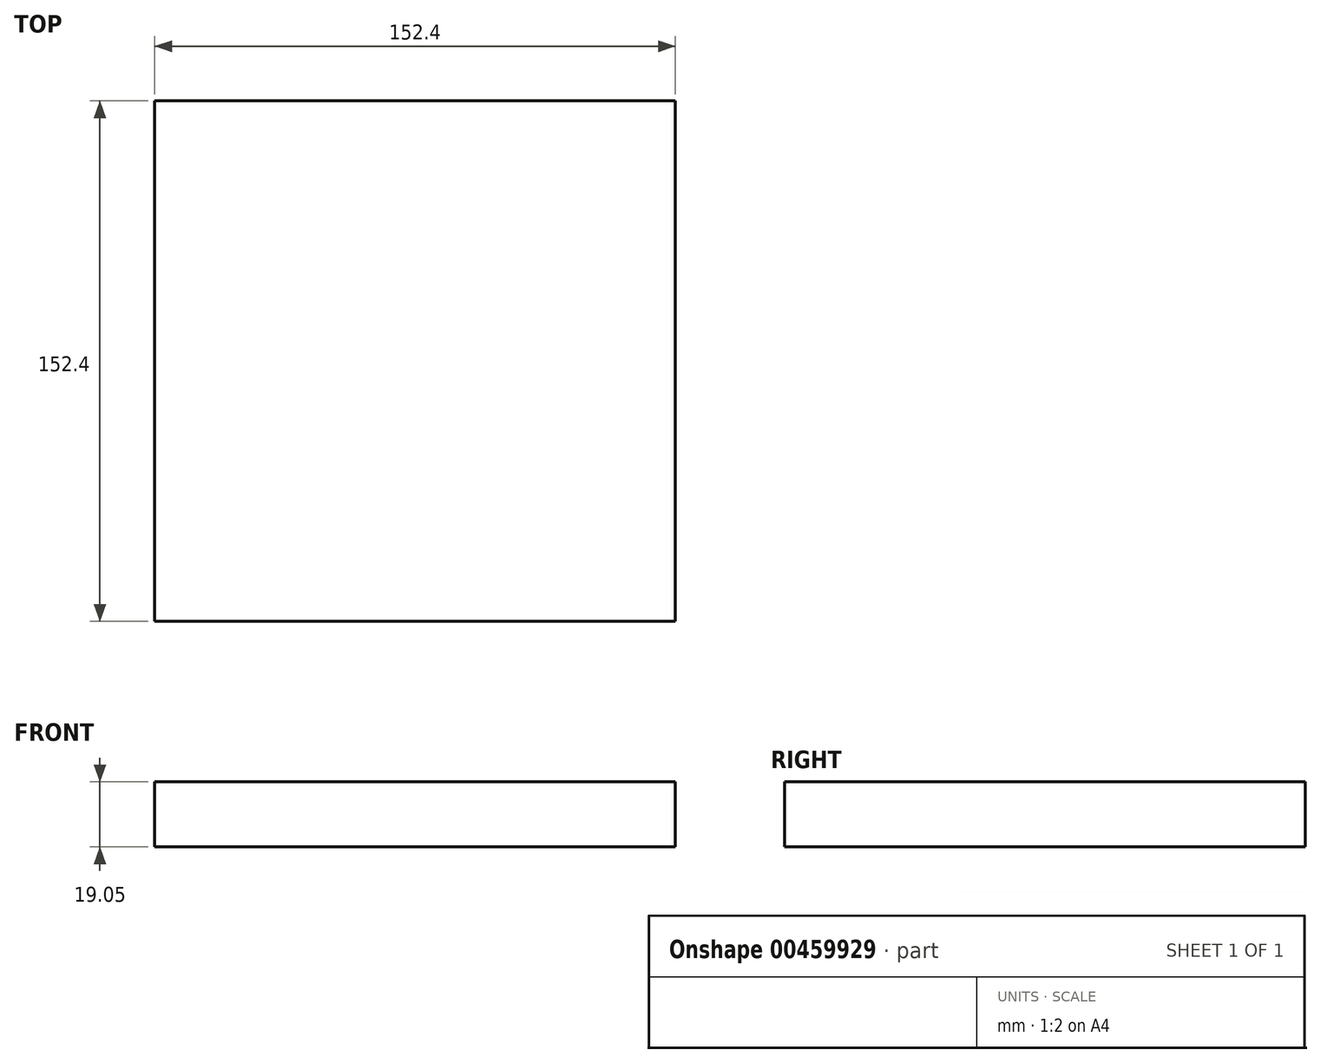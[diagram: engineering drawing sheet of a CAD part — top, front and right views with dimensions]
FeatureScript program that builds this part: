
annotation { "Feature Type Name" : "Feature", "Feature Type Description" : "" }
export const myFeature = defineFeature(function(context is Context, id is Id, definition is map)
    precondition{}
    {
        {
            var Q0;
            Q0=qCreatedBy(makeId("Top.planeOp"),FACE);
            var sketch = newSketch(context, id + "F0", { "sketchPlane" : qUnion([Q0])});
            skLineSegment(sketch, "E0.bottom", {"start": v(76.2, 76.2) * mm, "end": v(-76.2, 76.2) * mm});
            skLineSegment(sketch, "E0.top", {"start": v(76.2, -76.2) * mm, "end": v(-76.2, -76.2) * mm});
            skLineSegment(sketch, "E0.left", {"start": v(76.2, 76.2) * mm, "end": v(76.2, -76.2) * mm});
            skLineSegment(sketch, "E0.right", {"start": v(-76.2, 76.2) * mm, "end": v(-76.2, -76.2) * mm});
            skPoint(sketch, "E0.middle", {"position": v(0, 0) * mm});
            skSolve(sketch);
        }
        {
            var Q0;
            Q0=makeQuery(id+"F0.imprint","IMPRINT",FACE,{"disambiguationData":[TD([[makeQuery(id+"F0.imprint","IMPRINT",EDGE,{"derivedFrom":sQuery(id+"F0.wireOp",EDGE,"E0.bottom")}),1.0]])]});
            extrude(context, id + "F1", {"entities" : qUnion([Q0]), "depth" : 19.05 * mm});
        }
    });
